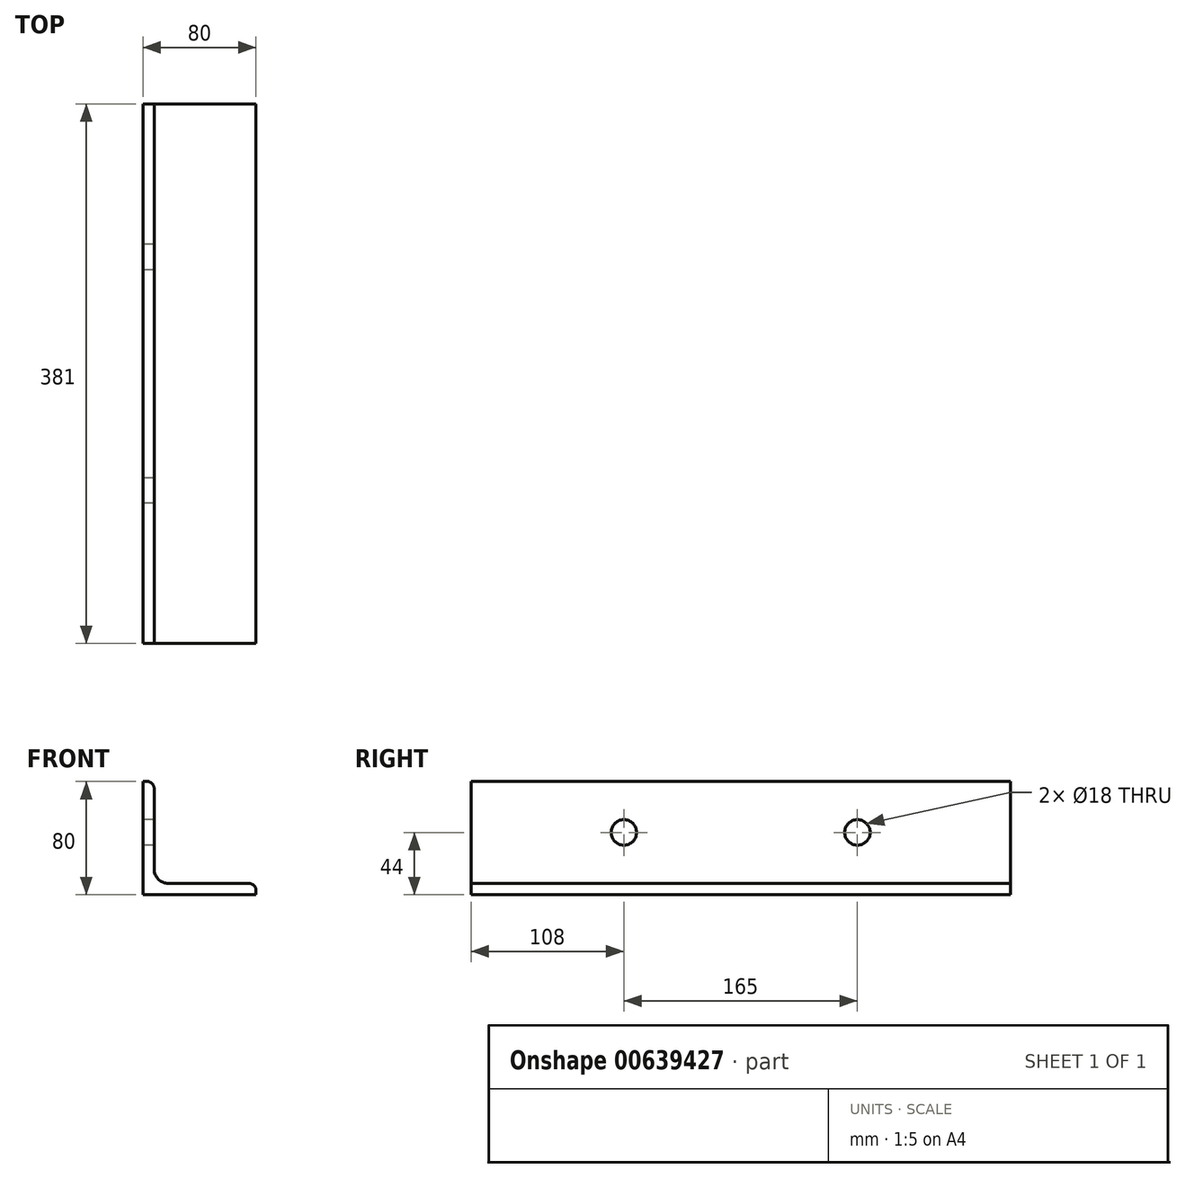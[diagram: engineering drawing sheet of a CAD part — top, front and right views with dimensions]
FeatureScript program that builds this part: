
annotation { "Feature Type Name" : "Feature", "Feature Type Description" : "" }
export const myFeature = defineFeature(function(context is Context, id is Id, definition is map)
    precondition{}
    {
        {
            var Q0;
            Q0=qCreatedBy(makeId("Front.planeOp"),FACE);
            var sketch = newSketch(context, id + "F0", { "sketchPlane" : qUnion([Q0])});
            skLineSegment(sketch, "E0", {"start": v(-28.3, 46.52) * mm, "end": v(-28.3, -33.48) * mm});
            skLineSegment(sketch, "E1", {"start": v(-28.3, -33.48) * mm, "end": v(51.7, -33.48) * mm});
            skLineSegment(sketch, "E2.0", {"start": v(-10.3, -25.48) * mm, "end": v(46.7, -25.48) * mm});
            skLineSegment(sketch, "E2.1", {"start": v(-20.3, 41.52) * mm, "end": v(-20.3, -15.48) * mm});
            skLineSegment(sketch, "E3", {"start": v(-28.3, 46.52) * mm, "end": v(-25.3, 46.52) * mm});
            skLineSegment(sketch, "E4", {"start": v(51.7, -30.48) * mm, "end": v(51.7, -33.48) * mm});
            skPoint(sketch, "E5.visualSharp", {"position": v(-20.3, -25.48) * mm});
            skArc(sketch, "E5.filletArc", {"start": v(-20.3, -15.48) * mm, "mid": v(-17.37, -22.55) * mm, "end": v(-10.3, -25.48) * mm});
            skPoint(sketch, "E6.visualSharp", {"position": v(-20.3, 46.52) * mm});
            skArc(sketch, "E6.filletArc", {"start": v(-20.3, 41.52) * mm, "mid": v(-21.76, 45.06) * mm, "end": v(-25.3, 46.52) * mm});
            skPoint(sketch, "E7.visualSharp", {"position": v(51.7, -25.48) * mm});
            skArc(sketch, "E7.filletArc", {"start": v(51.7, -30.48) * mm, "mid": v(50.24, -26.94) * mm, "end": v(46.7, -25.48) * mm});
            skSolve(sketch);
        }
        {
            var Q0;
            Q0=makeQuery(id+"F0.imprint","IMPRINT",FACE,{"disambiguationData":[TD([[makeQuery(id+"F0.imprint","IMPRINT",EDGE,{"derivedFrom":sQuery(id+"F0.wireOp",EDGE,"E0")}),1.0]])]});
            extrude(context, id + "F1", {"entities" : qUnion([Q0]), "depth" : 381 * mm, "offsetDistance" : 25 * mm});
        }
        {
            var Q0;
            Q0=makeQuery(id+"F1.opExtrude","SWEPT_FACE",FACE,{"disambiguationData":[OSD([sQuery(id+"F0.wireOp",EDGE,"E0")])]});
            var sketch = newSketch(context, id + "F2", { "sketchPlane" : qUnion([Q0])});
            skLineSegment(sketch, "E8.0", {"start": v(381, 46.52) * mm, "end": v(0, 46.52) * mm});
            skLineSegment(sketch, "E9", {"start": v(190.5, 46.52) * mm, "end": v(190.5, 10.52) * mm});
            skLineSegment(sketch, "E10.0", {"start": v(108, 46.52) * mm, "end": v(108, 10.52) * mm});
            skLineSegment(sketch, "E11.0", {"start": v(273, 46.52) * mm, "end": v(273, 10.52) * mm});
            skCircle(sketch, "E12", {"center": v(108, 10.52) * mm, "radius": 9 * mm});
            skCircle(sketch, "E13", {"center": v(273, 10.52) * mm, "radius": 9 * mm});
            skSolve(sketch);
        }
        {
            var Q0;
            Q0=makeQuery(id+"F2.imprint","IMPRINT",FACE,{"disambiguationData":[TD([[makeQuery(id+"F2.imprint","IMPRINT",EDGE,{"derivedFrom":sQuery(id+"F2.wireOp",EDGE,"E12")}),1.0]])]});
            var Q1;
            Q1=makeQuery(id+"F2.imprint","IMPRINT",FACE,{"disambiguationData":[TD([[makeQuery(id+"F2.imprint","IMPRINT",EDGE,{"derivedFrom":sQuery(id+"F2.wireOp",EDGE,"E13")}),1.0]])]});
            extrude(context, id + "F3", {"entities" : qUnion([Q0, Q1]), "operationType" : NewBodyOperationType.REMOVE, "endBound" : BoundingType.UP_TO_NEXT, "oppositeDirection" : true, "depth" : 25 * mm, "offsetDistance" : 25 * mm});
        }
    });
